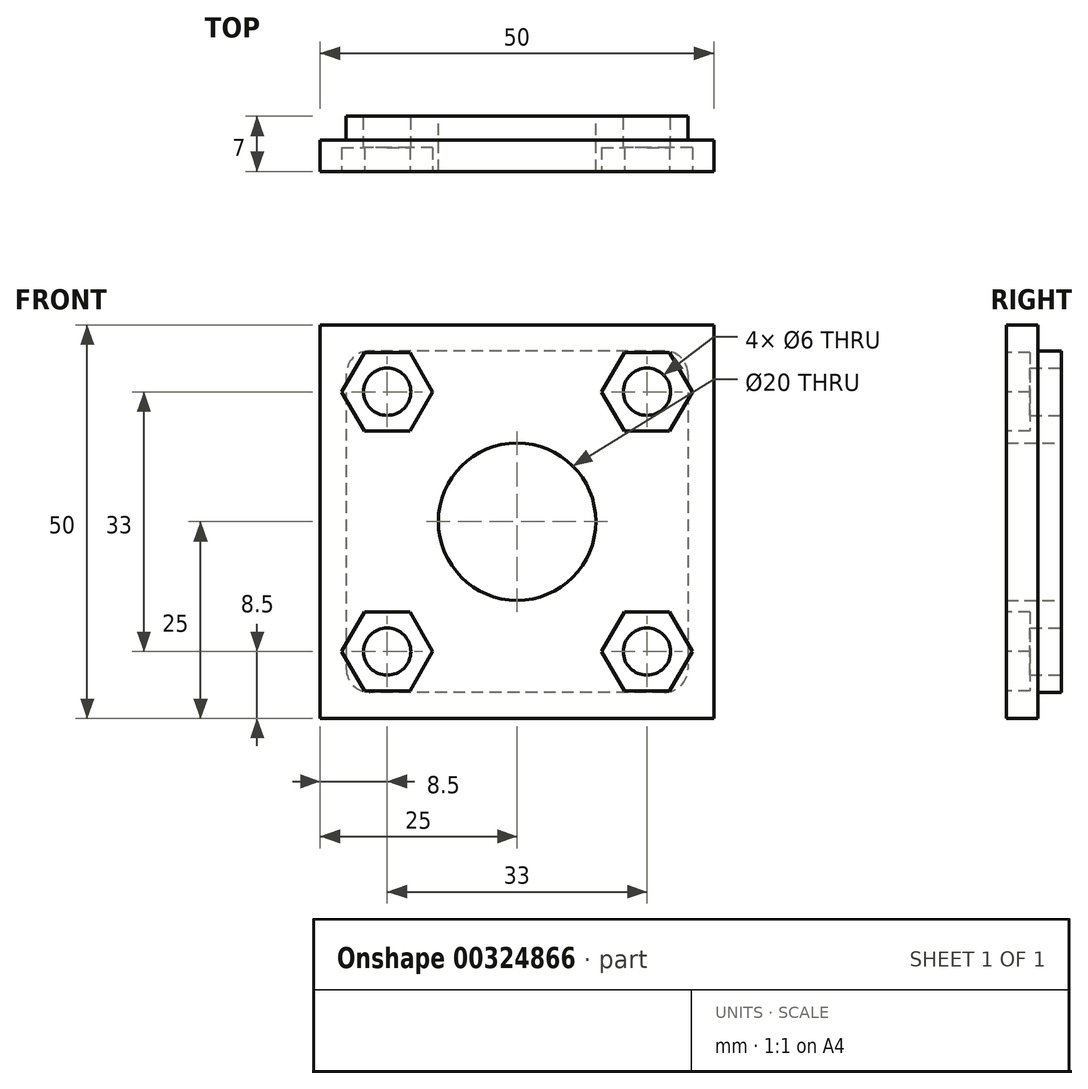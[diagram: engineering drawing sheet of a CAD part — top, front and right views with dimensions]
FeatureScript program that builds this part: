
annotation { "Feature Type Name" : "Feature", "Feature Type Description" : "" }
export const myFeature = defineFeature(function(context is Context, id is Id, definition is map)
    precondition{}
    {
        {
            var Q0;
            Q0=qCreatedBy(makeId("Front.planeOp"),FACE);
            var sketch = newSketch(context, id + "F0", { "sketchPlane" : qUnion([Q0])});
            skLineSegment(sketch, "E0.bottom", {"start": v(-25, 25) * mm, "end": v(25, 25) * mm});
            skLineSegment(sketch, "E0.top", {"start": v(-25, -25) * mm, "end": v(25, -25) * mm});
            skLineSegment(sketch, "E0.left", {"start": v(-25, 25) * mm, "end": v(-25, -25) * mm});
            skLineSegment(sketch, "E0.right", {"start": v(25, 25) * mm, "end": v(25, -25) * mm});
            skPoint(sketch, "E0.middle", {"position": v(0, 0) * mm});
            skSolve(sketch);
        }
        {
            var Q0;
            Q0=makeQuery(id+"F0.imprint","IMPRINT",FACE,{"disambiguationData":[TD([[makeQuery(id+"F0.imprint","IMPRINT",EDGE,{"derivedFrom":sQuery(id+"F0.wireOp",EDGE,"E0.bottom")}),-1.0]])]});
            extrude(context, id + "F1", {"entities" : qUnion([Q0]), "oppositeDirection" : true, "depth" : 4 * mm});
        }
        {
            var Q0;
            Q0=makeQuery(id+"F1.opExtrude","CAP_FACE",FACE,{"disambiguationData":[OSD([sQuery(id+"F0.wireOp",EDGE,"E0.bottom"),sQuery(id+"F0.wireOp",EDGE,"E0.top"),sQuery(id+"F0.wireOp",EDGE,"E0.left"),sQuery(id+"F0.wireOp",EDGE,"E0.right")])],"isStart":false});
            var sketch = newSketch(context, id + "F2", { "sketchPlane" : qUnion([Q0])});
            skLineSegment(sketch, "E1.bottom", {"start": v(-21.7, 21.7) * mm, "end": v(21.7, 21.7) * mm});
            skLineSegment(sketch, "E1.top", {"start": v(-21.7, -21.7) * mm, "end": v(21.7, -21.7) * mm});
            skLineSegment(sketch, "E1.left", {"start": v(-21.7, 21.7) * mm, "end": v(-21.7, -21.7) * mm});
            skLineSegment(sketch, "E1.right", {"start": v(21.7, 21.7) * mm, "end": v(21.7, -21.7) * mm});
            skPoint(sketch, "E1.middle", {"position": v(0, 0) * mm});
            skSolve(sketch);
        }
        {
            var Q0;
            Q0=makeQuery(id+"F2.imprint","IMPRINT",FACE,{"disambiguationData":[TD([[makeQuery(id+"F2.imprint","IMPRINT",EDGE,{"derivedFrom":sQuery(id+"F2.wireOp",EDGE,"E1.bottom")}),-1.0]])]});
            extrude(context, id + "F3", {"entities" : qUnion([Q0]), "operationType" : NewBodyOperationType.ADD, "depth" : 3 * mm});
        }
        {
            var Q0;
            Q0=makeQuery(id+"F3.opExtrude","CAP_FACE",FACE,{"disambiguationData":[OSD([sQuery(id+"F2.wireOp",EDGE,"E1.bottom"),sQuery(id+"F2.wireOp",EDGE,"E1.top"),sQuery(id+"F2.wireOp",EDGE,"E1.left"),sQuery(id+"F2.wireOp",EDGE,"E1.right")])],"isStart":false});
            var sketch = newSketch(context, id + "F4", { "sketchPlane" : qUnion([Q0])});
            skLineSegment(sketch, "E2", {"start": v(-21.7, 21.7) * mm, "end": v(21.7, -21.7) * mm, "construction": true});
            skLineSegment(sketch, "E3", {"start": v(21.7, 21.7) * mm, "end": v(-21.7, -21.7) * mm, "construction": true});
            skLineSegment(sketch, "E4.bottom", {"start": v(-16.5, 16.5) * mm, "end": v(16.5, 16.5) * mm, "construction": true});
            skLineSegment(sketch, "E4.top", {"start": v(-16.5, -16.5) * mm, "end": v(16.5, -16.5) * mm, "construction": true});
            skLineSegment(sketch, "E4.left", {"start": v(-16.5, 16.5) * mm, "end": v(-16.5, -16.5) * mm, "construction": true});
            skLineSegment(sketch, "E4.right", {"start": v(16.5, 16.5) * mm, "end": v(16.5, -16.5) * mm, "construction": true});
            skPoint(sketch, "E4.middle", {"position": v(0, 0) * mm});
            skCircle(sketch, "E5", {"center": v(-16.5, 16.5) * mm, "radius": 3 * mm});
            skCircle(sketch, "E6", {"center": v(16.5, 16.5) * mm, "radius": 3 * mm});
            skCircle(sketch, "E7", {"center": v(-16.5, -16.5) * mm, "radius": 3 * mm});
            skCircle(sketch, "E8", {"center": v(16.5, -16.5) * mm, "radius": 3 * mm});
            skCircle(sketch, "E9", {"center": v(0, 0) * mm, "radius": 10 * mm});
            skSolve(sketch);
        }
        {
            var Q0;
            Q0=makeQuery(id+"F4.imprint","IMPRINT",FACE,{"disambiguationData":[TD([[makeQuery(id+"F4.imprint","IMPRINT",EDGE,{"derivedFrom":sQuery(id+"F4.wireOp",EDGE,"E5")}),1.0]])]});
            var Q1;
            Q1=makeQuery(id+"F4.imprint","IMPRINT",FACE,{"disambiguationData":[TD([[makeQuery(id+"F4.imprint","IMPRINT",EDGE,{"derivedFrom":sQuery(id+"F4.wireOp",EDGE,"E6")}),1.0]])]});
            var Q2;
            Q2=makeQuery(id+"F4.imprint","IMPRINT",FACE,{"disambiguationData":[TD([[makeQuery(id+"F4.imprint","IMPRINT",EDGE,{"derivedFrom":sQuery(id+"F4.wireOp",EDGE,"E8")}),1.0]])]});
            var Q3;
            Q3=makeQuery(id+"F4.imprint","IMPRINT",FACE,{"disambiguationData":[TD([[makeQuery(id+"F4.imprint","IMPRINT",EDGE,{"derivedFrom":sQuery(id+"F4.wireOp",EDGE,"E7")}),1.0]])]});
            var Q4;
            Q4=makeQuery(id+"F4.imprint","IMPRINT",FACE,{"disambiguationData":[TD([[makeQuery(id+"F4.imprint","IMPRINT",EDGE,{"derivedFrom":sQuery(id+"F4.wireOp",EDGE,"E9")}),1.0]])]});
            extrude(context, id + "F5", {"entities" : qUnion([Q0, Q1, Q2, Q3, Q4]), "operationType" : NewBodyOperationType.REMOVE, "oppositeDirection" : true, "depth" : 25 * mm});
        }
        {
            var Q0;
            Q0=makeQuery(id+"F1.opExtrude","CAP_FACE",FACE,{"disambiguationData":[OSD([sQuery(id+"F0.wireOp",EDGE,"E0.bottom"),sQuery(id+"F0.wireOp",EDGE,"E0.top"),sQuery(id+"F0.wireOp",EDGE,"E0.left"),sQuery(id+"F0.wireOp",EDGE,"E0.right")])],"isStart":true});
            var sketch = newSketch(context, id + "F6", { "sketchPlane" : qUnion([Q0])});
            skCircle(sketch, "E10.cCircle", {"center": v(-16.5, 16.5) * mm, "radius": 5 * mm, "construction": true});
            skLineSegment(sketch, "E10.0", {"start": v(-13.61, 11.5) * mm, "end": v(-19.39, 11.5) * mm});
            skLineSegment(sketch, "E10.1", {"start": v(-19.39, 11.5) * mm, "end": v(-22.27, 16.5) * mm});
            skLineSegment(sketch, "E10.2", {"start": v(-22.27, 16.5) * mm, "end": v(-19.39, 21.5) * mm});
            skLineSegment(sketch, "E10.3", {"start": v(-19.39, 21.5) * mm, "end": v(-13.61, 21.5) * mm});
            skLineSegment(sketch, "E10.4", {"start": v(-13.61, 21.5) * mm, "end": v(-10.73, 16.5) * mm});
            skLineSegment(sketch, "E10.5", {"start": v(-10.73, 16.5) * mm, "end": v(-13.61, 11.5) * mm});
            skPoint(sketch, "E10.0.midPoint", {"position": v(-16.5, 11.5) * mm});
            skCircle(sketch, "E11.cCircle", {"center": v(-16.5, -16.5) * mm, "radius": 5 * mm, "construction": true});
            skLineSegment(sketch, "E11.0", {"start": v(-13.61, -21.5) * mm, "end": v(-19.39, -21.5) * mm});
            skLineSegment(sketch, "E11.1", {"start": v(-19.39, -21.5) * mm, "end": v(-22.27, -16.5) * mm});
            skLineSegment(sketch, "E11.2", {"start": v(-22.27, -16.5) * mm, "end": v(-19.39, -11.5) * mm});
            skLineSegment(sketch, "E11.3", {"start": v(-19.39, -11.5) * mm, "end": v(-13.61, -11.5) * mm});
            skLineSegment(sketch, "E11.4", {"start": v(-13.61, -11.5) * mm, "end": v(-10.73, -16.5) * mm});
            skLineSegment(sketch, "E11.5", {"start": v(-10.73, -16.5) * mm, "end": v(-13.61, -21.5) * mm});
            skPoint(sketch, "E11.0.midPoint", {"position": v(-16.5, -21.5) * mm});
            skCircle(sketch, "E12.cCircle", {"center": v(16.5, 16.5) * mm, "radius": 5 * mm, "construction": true});
            skLineSegment(sketch, "E12.0", {"start": v(13.61, 21.5) * mm, "end": v(19.39, 21.5) * mm});
            skLineSegment(sketch, "E12.1", {"start": v(19.39, 21.5) * mm, "end": v(22.27, 16.5) * mm});
            skLineSegment(sketch, "E12.2", {"start": v(22.27, 16.5) * mm, "end": v(19.39, 11.5) * mm});
            skLineSegment(sketch, "E12.3", {"start": v(19.39, 11.5) * mm, "end": v(13.61, 11.5) * mm});
            skLineSegment(sketch, "E12.4", {"start": v(13.61, 11.5) * mm, "end": v(10.73, 16.5) * mm});
            skLineSegment(sketch, "E12.5", {"start": v(10.73, 16.5) * mm, "end": v(13.61, 21.5) * mm});
            skPoint(sketch, "E12.0.midPoint", {"position": v(16.5, 21.5) * mm});
            skCircle(sketch, "E13.cCircle", {"center": v(16.5, -16.5) * mm, "radius": 5 * mm, "construction": true});
            skLineSegment(sketch, "E13.0", {"start": v(19.39, -21.5) * mm, "end": v(13.61, -21.5) * mm});
            skLineSegment(sketch, "E13.1", {"start": v(13.61, -21.5) * mm, "end": v(10.73, -16.5) * mm});
            skLineSegment(sketch, "E13.2", {"start": v(10.73, -16.5) * mm, "end": v(13.61, -11.5) * mm});
            skLineSegment(sketch, "E13.3", {"start": v(13.61, -11.5) * mm, "end": v(19.39, -11.5) * mm});
            skLineSegment(sketch, "E13.4", {"start": v(19.39, -11.5) * mm, "end": v(22.27, -16.5) * mm});
            skLineSegment(sketch, "E13.5", {"start": v(22.27, -16.5) * mm, "end": v(19.39, -21.5) * mm});
            skPoint(sketch, "E13.0.midPoint", {"position": v(16.5, -21.5) * mm});
            skSolve(sketch);
        }
        {
            var Q0;
            Q0=makeQuery(id+"F6.imprint","IMPRINT",FACE,{"disambiguationData":[TD([[makeQuery(id+"F6.imprint","IMPRINT",EDGE,{"derivedFrom":sQuery(id+"F6.wireOp",EDGE,"E10.0")}),-1.0]])]});
            var Q1;
            Q1=makeQuery(id+"F6.imprint","IMPRINT",FACE,{"disambiguationData":[TD([[makeQuery(id+"F6.imprint","IMPRINT",EDGE,{"derivedFrom":sQuery(id+"F6.wireOp",EDGE,"E12.0")}),-1.0]])]});
            var Q2;
            Q2=makeQuery(id+"F6.imprint","IMPRINT",FACE,{"disambiguationData":[TD([[makeQuery(id+"F6.imprint","IMPRINT",EDGE,{"derivedFrom":sQuery(id+"F6.wireOp",EDGE,"E13.0")}),-1.0]])]});
            var Q3;
            Q3=makeQuery(id+"F6.imprint","IMPRINT",FACE,{"disambiguationData":[TD([[makeQuery(id+"F6.imprint","IMPRINT",EDGE,{"derivedFrom":sQuery(id+"F6.wireOp",EDGE,"E11.0")}),-1.0]])]});
            extrude(context, id + "F7", {"entities" : qUnion([Q0, Q1, Q2, Q3]), "operationType" : NewBodyOperationType.REMOVE, "oppositeDirection" : true, "depth" : 3 * mm});
        }
        {
            var Q0;
            Q0=makeQuery(id+"F3.opExtrude","SWEPT_EDGE",EDGE,{"disambiguationData":[OSD([sQuery(id+"F2.wireOp",EDGE,"E1.bottom"),sQuery(id+"F2.wireOp",EDGE,"E1.left")])]});
            var Q1;
            Q1=makeQuery(id+"F3.opExtrude","SWEPT_EDGE",EDGE,{"disambiguationData":[OSD([sQuery(id+"F2.wireOp",EDGE,"E1.bottom"),sQuery(id+"F2.wireOp",EDGE,"E1.right")])]});
            var Q2;
            Q2=makeQuery(id+"F3.opExtrude","SWEPT_EDGE",EDGE,{"disambiguationData":[OSD([sQuery(id+"F2.wireOp",EDGE,"E1.top"),sQuery(id+"F2.wireOp",EDGE,"E1.right")])]});
            var Q3;
            Q3=makeQuery(id+"F3.opExtrude","SWEPT_EDGE",EDGE,{"disambiguationData":[OSD([sQuery(id+"F2.wireOp",EDGE,"E1.top"),sQuery(id+"F2.wireOp",EDGE,"E1.left")])]});
            fillet(context, id + "F8", {"entities" : qUnion([Q0, Q1, Q2, Q3]), "radius" : 3 * mm, "tangentPropagation" : true, "allowEdgeOverflow" : false});
        }
    });
